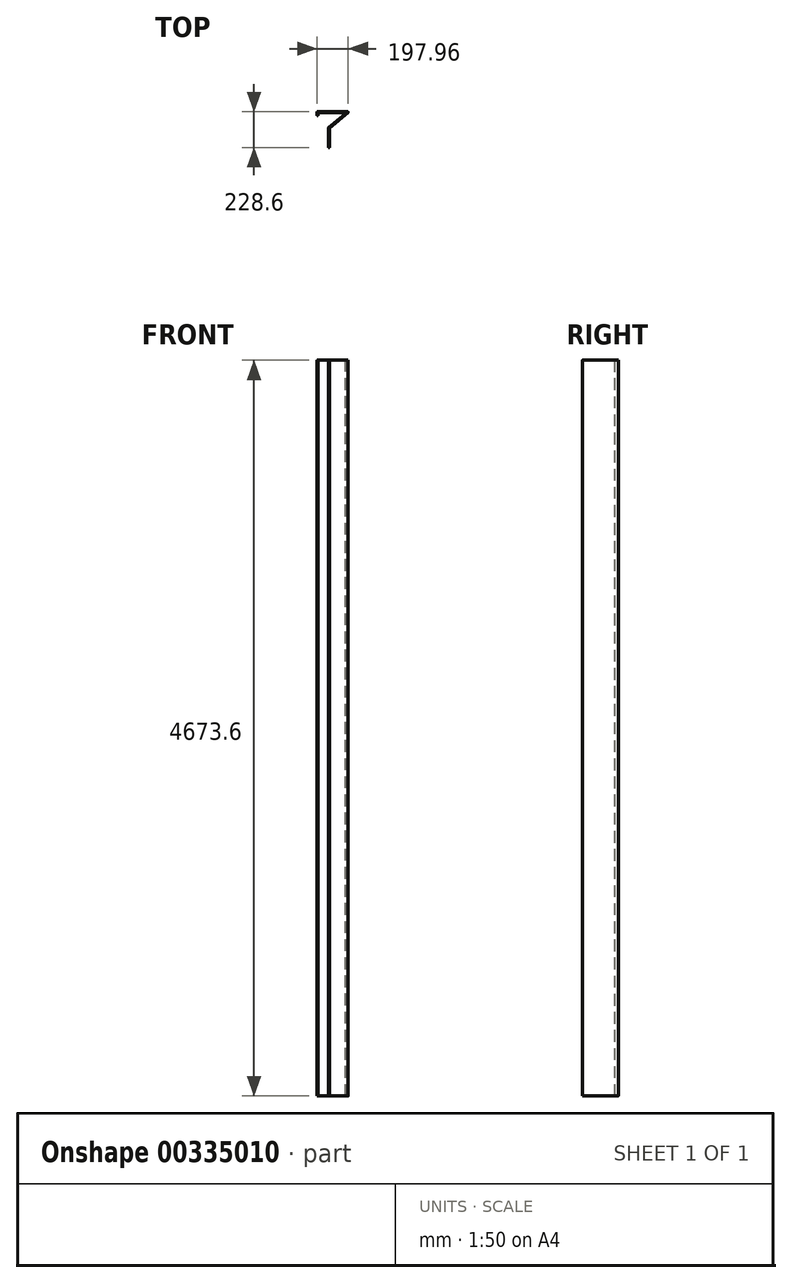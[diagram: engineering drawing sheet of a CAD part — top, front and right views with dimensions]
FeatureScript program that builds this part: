
annotation { "Feature Type Name" : "Feature", "Feature Type Description" : "" }
export const myFeature = defineFeature(function(context is Context, id is Id, definition is map)
    precondition{}
    {
        {
            var Q0;
            Q0=qCreatedBy(makeId("Top.planeOp"),FACE);
            var sketch = newSketch(context, id + "F0", { "sketchPlane" : qUnion([Q0])});
            skLineSegment(sketch, "E0", {"start": v(0, 0) * mm, "end": v(0, 127) * mm});
            skLineSegment(sketch, "E1", {"start": v(0, 127) * mm, "end": v(113.51, 222.25) * mm});
            skLineSegment(sketch, "E2", {"start": v(113.51, 222.25) * mm, "end": v(-65.89, 222.25) * mm});
            skLineSegment(sketch, "E3", {"start": v(-65.89, 222.25) * mm, "end": v(-65.89, 203.2) * mm});
            skLineSegment(sketch, "E4", {"start": v(-65.89, 203.2) * mm, "end": v(-72.24, 203.2) * mm});
            skLineSegment(sketch, "E5", {"start": v(-72.24, 203.2) * mm, "end": v(-72.24, 228.6) * mm});
            skLineSegment(sketch, "E6", {"start": v(-72.24, 228.6) * mm, "end": v(130.96, 228.6) * mm});
            skLineSegment(sketch, "E7", {"start": v(130.96, 228.6) * mm, "end": v(6.35, 124.04) * mm});
            skLineSegment(sketch, "E8", {"start": v(6.35, 124.04) * mm, "end": v(6.35, 0) * mm});
            skLineSegment(sketch, "E9", {"start": v(6.35, 0) * mm, "end": v(0, 0) * mm});
            skLineSegment(sketch, "E10", {"start": v(-14.53, 133.77) * mm, "end": v(1.18, 126.45) * mm, "construction": true});
            skSolve(sketch);
        }
        {
            var Q0;
            Q0 = qSketchRegion(id + "F0", true);
            extrude(context, id + "F1", {"entities" : qUnion([Q0]), "depth" : 4673.6 * mm});
        }
        {
            var Q0;
            Q0=makeQuery(id+"F1.opExtrude","SWEPT_EDGE",EDGE,{"disambiguationData":[OSD([sQuery(id+"F0.wireOp",EDGE,"E4"),sQuery(id+"F0.wireOp",EDGE,"E5")])]});
            var Q1;
            Q1=makeQuery(id+"F1.opExtrude","SWEPT_EDGE",EDGE,{"disambiguationData":[OSD([sQuery(id+"F0.wireOp",EDGE,"E5"),sQuery(id+"F0.wireOp",EDGE,"E6")])]});
            var Q2;
            Q2=makeQuery(id+"F1.opExtrude","SWEPT_EDGE",EDGE,{"disambiguationData":[OSD([sQuery(id+"F0.wireOp",EDGE,"E6"),sQuery(id+"F0.wireOp",EDGE,"E7")])]});
            var Q3;
            Q3=makeQuery(id+"F1.opExtrude","SWEPT_EDGE",EDGE,{"disambiguationData":[OSD([sQuery(id+"F0.wireOp",EDGE,"E0"),sQuery(id+"F0.wireOp",EDGE,"E9")])]});
            var Q4;
            Q4=makeQuery(id+"F1.opExtrude","SWEPT_EDGE",EDGE,{"disambiguationData":[OSD([sQuery(id+"F0.wireOp",EDGE,"E8"),sQuery(id+"F0.wireOp",EDGE,"E9")])]});
            var Q5;
            Q5=makeQuery(id+"F1.opExtrude","SWEPT_EDGE",EDGE,{"disambiguationData":[OSD([sQuery(id+"F0.wireOp",EDGE,"E0"),sQuery(id+"F0.wireOp",EDGE,"E1")])]});
            var Q6;
            Q6=makeQuery(id+"F1.opExtrude","SWEPT_EDGE",EDGE,{"disambiguationData":[OSD([sQuery(id+"F0.wireOp",EDGE,"E7"),sQuery(id+"F0.wireOp",EDGE,"E8")])]});
            var Q7;
            Q7=makeQuery(id+"F1.opExtrude","SWEPT_EDGE",EDGE,{"disambiguationData":[OSD([sQuery(id+"F0.wireOp",EDGE,"E1"),sQuery(id+"F0.wireOp",EDGE,"E2")])]});
            var Q8;
            Q8=makeQuery(id+"F1.opExtrude","SWEPT_EDGE",EDGE,{"disambiguationData":[OSD([sQuery(id+"F0.wireOp",EDGE,"E2"),sQuery(id+"F0.wireOp",EDGE,"E3")])]});
            var Q9;
            Q9=makeQuery(id+"F1.opExtrude","SWEPT_EDGE",EDGE,{"disambiguationData":[OSD([sQuery(id+"F0.wireOp",EDGE,"E3"),sQuery(id+"F0.wireOp",EDGE,"E4")])]});
            fillet(context, id + "F2", {"entities" : qUnion([Q0, Q1, Q2, Q3, Q4, Q5, Q6, Q7, Q8, Q9]), "radius" : 3 * mm, "tangentPropagation" : true, "allowEdgeOverflow" : false});
        }
    });
